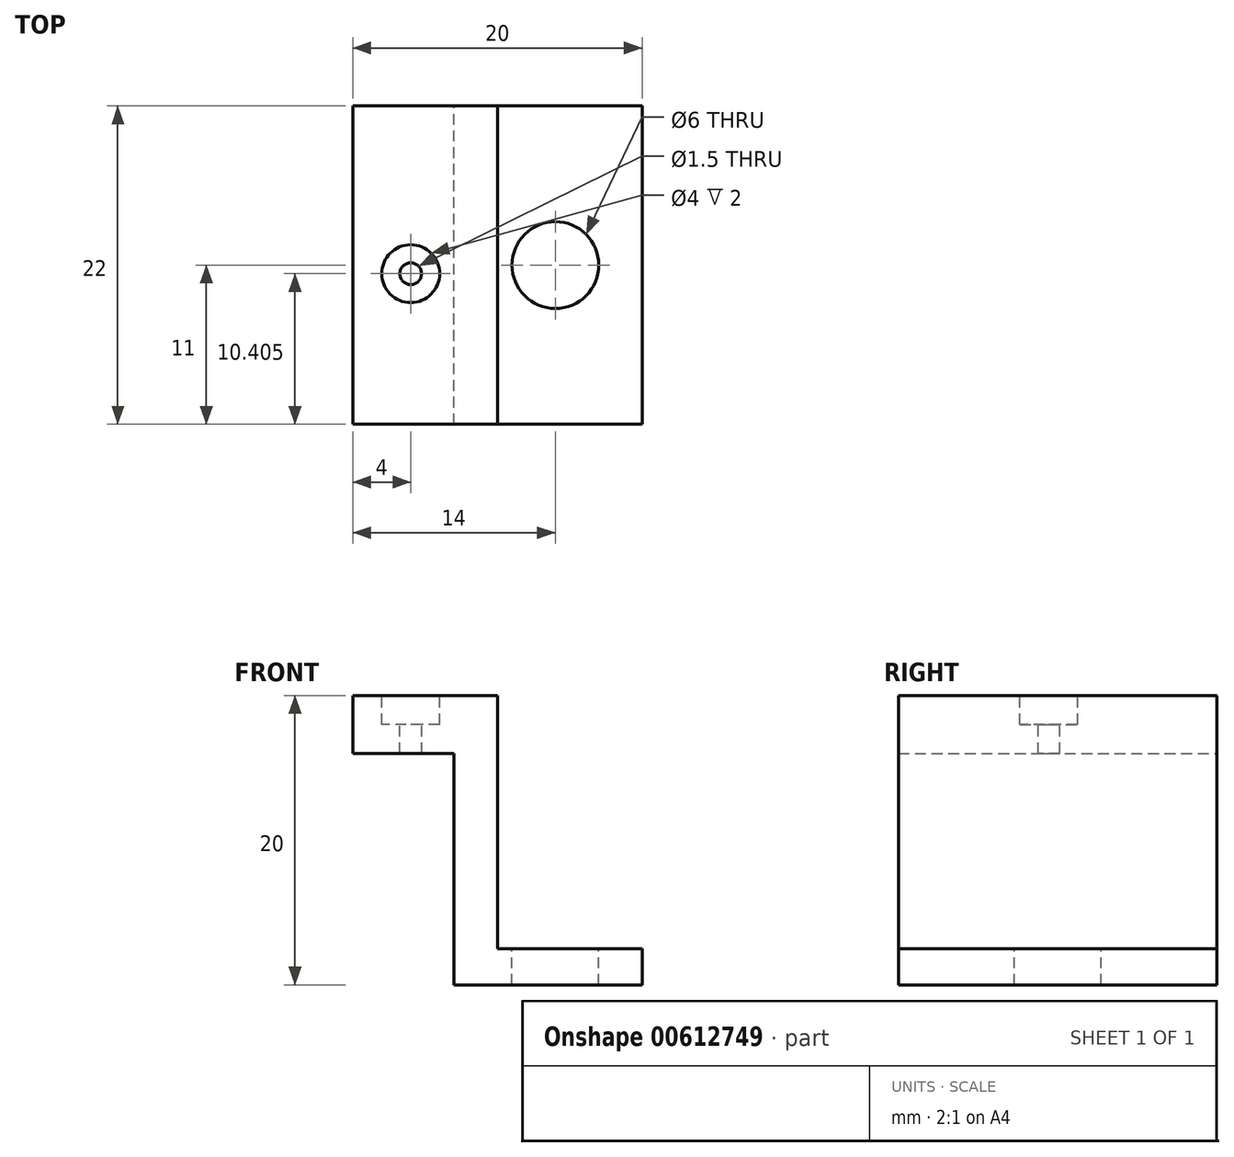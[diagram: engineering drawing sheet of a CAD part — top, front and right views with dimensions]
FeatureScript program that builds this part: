
annotation { "Feature Type Name" : "Feature", "Feature Type Description" : "" }
export const myFeature = defineFeature(function(context is Context, id is Id, definition is map)
    precondition{}
    {
        {
            var Q0;
            Q0=qCreatedBy(makeId("Front.planeOp"),FACE);
            var sketch = newSketch(context, id + "F0", { "sketchPlane" : qUnion([Q0])});
            skLineSegment(sketch, "E0", {"start": v(0, 0) * mm, "end": v(0, 2.5) * mm});
            skLineSegment(sketch, "E1", {"start": v(0, 2.5) * mm, "end": v(-10, 2.5) * mm});
            skLineSegment(sketch, "E2", {"start": v(-10, 2.5) * mm, "end": v(-10, 20) * mm});
            skLineSegment(sketch, "E3", {"start": v(-10, 20) * mm, "end": v(-20, 20) * mm});
            skLineSegment(sketch, "E4", {"start": v(-20, 20) * mm, "end": v(-20, 16) * mm});
            skLineSegment(sketch, "E5", {"start": v(-20, 16) * mm, "end": v(-13, 16) * mm});
            skLineSegment(sketch, "E6", {"start": v(-13, 16) * mm, "end": v(-13, 0) * mm});
            skLineSegment(sketch, "E7", {"start": v(-13, 0) * mm, "end": v(0, 0) * mm});
            skSolve(sketch);
        }
        {
            var Q0;
            Q0=makeQuery(id+"F0.imprint","IMPRINT",FACE,{"disambiguationData":[TD([[makeQuery(id+"F0.imprint","IMPRINT",EDGE,{"derivedFrom":sQuery(id+"F0.wireOp",EDGE,"E0")}),1.0]])]});
            extrude(context, id + "F1", {"entities" : qUnion([Q0]), "depth" : 22 * mm, "offsetDistance" : 25 * mm});
        }
        {
            var Q0;
            Q0=makeQuery(id+"F1.opExtrude","SWEPT_FACE",FACE,{"disambiguationData":[OSD([sQuery(id+"F0.wireOp",EDGE,"E1")])]});
            var sketch = newSketch(context, id + "F2", { "sketchPlane" : qUnion([Q0])});
            skPoint(sketch, "E8", {"position": v(-6, -11) * mm});
            skSolve(sketch);
        }
        {
            var Q0;
            Q0=sQuery(id+"F2.wireOp",VERTEX,"E8");
            var Q1;
            Q1=makeQuery(id+"F1.opExtrude","SWEPT_BODY",BODY,{"disambiguationData":[OSD([sQuery(id+"F0.wireOp",EDGE,"E0"),sQuery(id+"F0.wireOp",EDGE,"E1"),sQuery(id+"F0.wireOp",EDGE,"E2"),sQuery(id+"F0.wireOp",EDGE,"E3"),sQuery(id+"F0.wireOp",EDGE,"E4"),sQuery(id+"F0.wireOp",EDGE,"E5"),sQuery(id+"F0.wireOp",EDGE,"E6"),sQuery(id+"F0.wireOp",EDGE,"E7")])]});
            hole(context, id + "F3", {"style" : HoleStyle.SIMPLE, "endStyle" : HoleEndStyle.THROUGH, "holeDiameter" : 6 * mm, "majorDiameter" : 5 * mm, "isTappedThrough" : true, "tappedDepth" : 12 * mm, "tapClearance" : 3, "locations" : qUnion([Q0]), "scope" : qUnion([Q1])});
        }
        {
            var Q0;
            Q0=makeQuery(id+"F1.opExtrude","SWEPT_FACE",FACE,{"disambiguationData":[OSD([sQuery(id+"F0.wireOp",EDGE,"E3")])]});
            var sketch = newSketch(context, id + "F4", { "sketchPlane" : qUnion([Q0])});
            skPoint(sketch, "E9", {"position": v(-16, -11.6) * mm});
            skSolve(sketch);
        }
        {
            var Q0;
            Q0=sQuery(id+"F4.wireOp",VERTEX,"E9");
            var Q1;
            Q1=makeQuery(id+"F1.opExtrude","SWEPT_BODY",BODY,{"disambiguationData":[OSD([sQuery(id+"F0.wireOp",EDGE,"E0"),sQuery(id+"F0.wireOp",EDGE,"E1"),sQuery(id+"F0.wireOp",EDGE,"E2"),sQuery(id+"F0.wireOp",EDGE,"E3"),sQuery(id+"F0.wireOp",EDGE,"E4"),sQuery(id+"F0.wireOp",EDGE,"E5"),sQuery(id+"F0.wireOp",EDGE,"E6"),sQuery(id+"F0.wireOp",EDGE,"E7")])]});
            hole(context, id + "F5", {"style" : HoleStyle.C_BORE, "endStyle" : HoleEndStyle.THROUGH, "holeDiameter" : 1.5 * mm, "cBoreDiameter" : 4 * mm, "cBoreDepth" : 2 * mm, "majorDiameter" : 5 * mm, "isTappedThrough" : true, "tappedDepth" : 12 * mm, "tapClearance" : 3, "locations" : qUnion([Q0]), "scope" : qUnion([Q1])});
        }
    });
